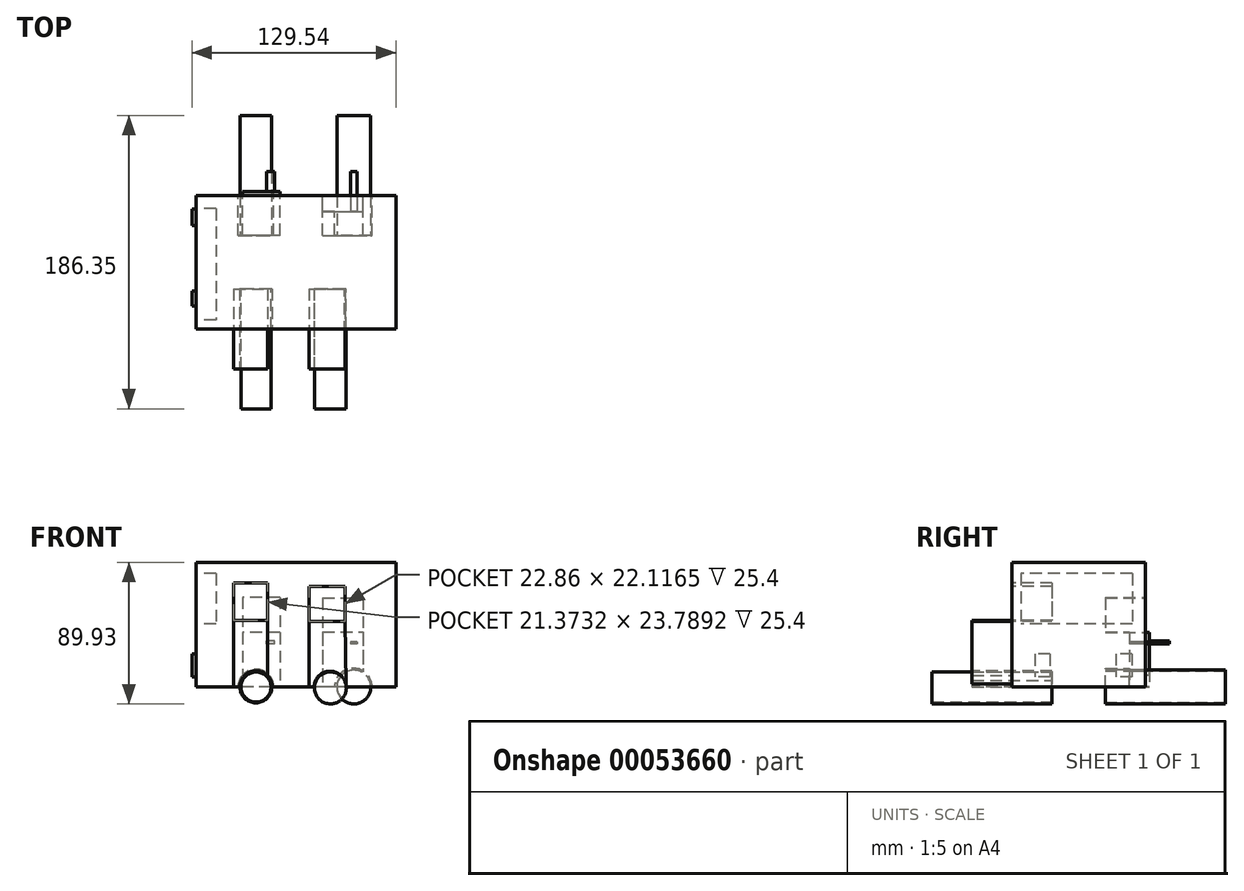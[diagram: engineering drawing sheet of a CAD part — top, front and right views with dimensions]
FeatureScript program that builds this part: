
annotation { "Feature Type Name" : "Feature", "Feature Type Description" : "" }
export const myFeature = defineFeature(function(context is Context, id is Id, definition is map)
    precondition{}
    {
        {
            var Q0;
            Q0=qCreatedBy(makeId("Right.planeOp"),FACE);
            var sketch = newSketch(context, id + "F0", { "sketchPlane" : qUnion([Q0])});
            skLineSegment(sketch, "E0.bottom", {"start": v(46.13, 54.55) * mm, "end": v(-38.62, 54.55) * mm});
            skLineSegment(sketch, "E0.top", {"start": v(46.13, -24.63) * mm, "end": v(-38.62, -24.63) * mm});
            skLineSegment(sketch, "E0.left", {"start": v(46.13, 54.55) * mm, "end": v(46.13, -24.63) * mm});
            skLineSegment(sketch, "E0.right", {"start": v(-38.62, 54.55) * mm, "end": v(-38.62, -24.63) * mm});
            skSolve(sketch);
        }
        {
            var Q0;
            Q0=makeQuery(id+"F0.imprint","IMPRINT",FACE,{"disambiguationData":[TD([[makeQuery(id+"F0.imprint","IMPRINT",EDGE,{"derivedFrom":sQuery(id+"F0.wireOp",EDGE,"E0.bottom")}),1.0]])]});
            extrude(context, id + "F1", {"entities" : qUnion([Q0]), "depth" : 127 * mm});
        }
        {
            var Q0;
            Q0=makeQuery(id+"F1.opExtrude","CAP_FACE",FACE,{"disambiguationData":[OSD([sQuery(id+"F0.wireOp",EDGE,"E0.bottom"),sQuery(id+"F0.wireOp",EDGE,"E0.top"),sQuery(id+"F0.wireOp",EDGE,"E0.left"),sQuery(id+"F0.wireOp",EDGE,"E0.right")])],"isStart":true});
            var sketch = newSketch(context, id + "F2", { "sketchPlane" : qUnion([Q0])});
            skLineSegment(sketch, "E1.bottom", {"start": v(-37.77, 47.49) * mm, "end": v(33.04, 47.49) * mm});
            skLineSegment(sketch, "E1.top", {"start": v(-37.77, 15.33) * mm, "end": v(33.04, 15.33) * mm});
            skLineSegment(sketch, "E1.left", {"start": v(-37.77, 47.49) * mm, "end": v(-37.77, 15.33) * mm});
            skLineSegment(sketch, "E1.right", {"start": v(33.04, 47.49) * mm, "end": v(33.04, 15.33) * mm});
            skSolve(sketch);
        }
        {
            var Q0;
            Q0=makeQuery(id+"F2.imprint","IMPRINT",FACE,{"disambiguationData":[TD([[makeQuery(id+"F2.imprint","IMPRINT",EDGE,{"derivedFrom":sQuery(id+"F2.wireOp",EDGE,"E1.bottom")}),-1.0]])]});
            extrude(context, id + "F3", {"entities" : qUnion([Q0]), "operationType" : NewBodyOperationType.REMOVE, "oppositeDirection" : true, "depth" : 12.7 * mm});
        }
        {
            var Q0;
            Q0=makeQuery(id+"F1.opExtrude","SWEPT_FACE",FACE,{"disambiguationData":[OSD([sQuery(id+"F0.wireOp",EDGE,"E0.left")])]});
            var sketch = newSketch(context, id + "F4", { "sketchPlane" : qUnion([Q0])});
            skCircle(sketch, "E2", {"center": v(-99.97, -24.63) * mm, "radius": 11.9 * mm});
            skCircle(sketch, "E3", {"center": v(-38.08, -24.63) * mm, "radius": 11.33 * mm});
            skLineSegment(sketch, "E4", {"start": v(-75.62, 13.1) * mm, "end": v(-75.62, -24.63) * mm});
            skLineSegment(sketch, "E5", {"start": v(-75.62, 13.1) * mm, "end": v(-75.62, 31.5) * mm});
            skLineSegment(sketch, "E6", {"start": v(-50.34, 30.39) * mm, "end": v(-49.4, -24.63) * mm});
            skLineSegment(sketch, "E7", {"start": v(-98.66, 30.39) * mm, "end": v(-98.66, -7.53) * mm});
            skLineSegment(sketch, "E8", {"start": v(-98.66, -7.53) * mm, "end": v(-98.66, -12.79) * mm});
            skSolve(sketch);
        }
        {
            var Q0;
            {var subQ0=sQuery(id+"F4.wireOp",EDGE,"E2");var subQ1=makeQuery(id+"F4.imprint","IMPRINT",VERTEX,{"derivedFrom":subQ0});Q0=makeQuery(id+"F4.imprint","IMPRINT",FACE,{"disambiguationData":[TD([[makeQuery(id+"F4.imprint","IMPRINT",EDGE,{"disambiguationData":[TD([[subQ1,1.0]])],"derivedFrom":subQ0}),1.0]])]});}
            var Q1;
            {var subQ0=sQuery(id+"F4.wireOp",EDGE,"E3");var subQ1=makeQuery(id+"F1.opExtrude","SWEPT_EDGE",EDGE,{"disambiguationData":[OSD([sQuery(id+"F0.wireOp",EDGE,"E0.top"),sQuery(id+"F0.wireOp",EDGE,"E0.left")])]});var subQ2=makeQuery(id+"F4.imprint","INTERSECT",VERTEX,{"disambiguationData":[OD(0.0)],"derivedFrom":[subQ1,subQ0]});Q1=makeQuery(id+"F4.imprint","IMPRINT",FACE,{"disambiguationData":[TD([[makeQuery(id+"F4.imprint","IMPRINT",EDGE,{"disambiguationData":[TD([[subQ2,-1.0]])],"derivedFrom":subQ0}),1.0]])]});}
            extrude(context, id + "F5", {"entities" : qUnion([Q0, Q1]), "operationType" : NewBodyOperationType.REMOVE, "oppositeDirection" : true, "depth" : 25.4 * mm});
        }
        {
            var Q0;
            Q0=makeQuery(id+"F1.opExtrude","SWEPT_FACE",FACE,{"disambiguationData":[OSD([sQuery(id+"F0.wireOp",EDGE,"E0.right")])]});
            var sketch = newSketch(context, id + "F6", { "sketchPlane" : qUnion([Q0])});
            skCircle(sketch, "E9", {"center": v(38.19, -24.63) * mm, "radius": 10.32 * mm});
            skCircle(sketch, "E10", {"center": v(85.2, -24.63) * mm, "radius": 10.06 * mm});
            skLineSegment(sketch, "E11", {"start": v(67, 17.75) * mm, "end": v(68.48, -24.63) * mm});
            skLineSegment(sketch, "E12", {"start": v(43.39, 16.82) * mm, "end": v(45.25, -14.22) * mm});
            skLineSegment(sketch, "E13", {"start": v(45.25, -14.22) * mm, "end": v(42.64, 29.28) * mm});
            skLineSegment(sketch, "E14", {"start": v(67, 17.75) * mm, "end": v(66.6, 29.13) * mm});
            skLineSegment(sketch, "E15", {"start": v(65.5, 29.83) * mm, "end": v(66.6, 29.13) * mm});
            skLineSegment(sketch, "E16", {"start": v(94.13, -19.99) * mm, "end": v(88.74, 26.86) * mm});
            skSolve(sketch);
        }
        {
            var Q0;
            {var subQ0=sQuery(id+"F6.wireOp",EDGE,"E9");var subQ1=makeQuery(id+"F1.opExtrude","SWEPT_EDGE",EDGE,{"disambiguationData":[OSD([sQuery(id+"F0.wireOp",EDGE,"E0.top"),sQuery(id+"F0.wireOp",EDGE,"E0.right")])]});var subQ2=makeQuery(id+"F6.imprint","INTERSECT",VERTEX,{"disambiguationData":[OD(0.0)],"derivedFrom":[subQ1,subQ0]});Q0=makeQuery(id+"F6.imprint","IMPRINT",FACE,{"disambiguationData":[TD([[makeQuery(id+"F6.imprint","IMPRINT",EDGE,{"disambiguationData":[TD([[subQ2,-1.0]])],"derivedFrom":subQ0}),1.0]])]});}
            var Q1;
            {var subQ0=sQuery(id+"F6.wireOp",EDGE,"E9");var subQ1=makeQuery(id+"F1.opExtrude","SWEPT_EDGE",EDGE,{"disambiguationData":[OSD([sQuery(id+"F0.wireOp",EDGE,"E0.top"),sQuery(id+"F0.wireOp",EDGE,"E0.right")])]});var subQ2=makeQuery(id+"F6.imprint","INTERSECT",VERTEX,{"disambiguationData":[OD(0.0)],"derivedFrom":[subQ1,subQ0]});Q1=makeQuery(id+"F6.imprint","IMPRINT",FACE,{"disambiguationData":[TD([[makeQuery(id+"F6.imprint","IMPRINT",EDGE,{"disambiguationData":[TD([[subQ2,1.0]])],"derivedFrom":subQ0}),1.0]])]});}
            var Q2;
            {var subQ0=sQuery(id+"F6.wireOp",EDGE,"E10");var subQ1=makeQuery(id+"F6.imprint","IMPRINT",VERTEX,{"derivedFrom":subQ0});Q2=makeQuery(id+"F6.imprint","IMPRINT",FACE,{"disambiguationData":[TD([[makeQuery(id+"F6.imprint","IMPRINT",EDGE,{"disambiguationData":[TD([[subQ1,1.0]])],"derivedFrom":subQ0}),1.0]])]});}
            extrude(context, id + "F7", {"entities" : qUnion([Q0, Q1, Q2]), "operationType" : NewBodyOperationType.REMOVE, "oppositeDirection" : true, "depth" : 25.4 * mm});
        }
        {
            var Q0;
            Q0=makeQuery(id+"F1.opExtrude","SWEPT_FACE",FACE,{"disambiguationData":[OSD([sQuery(id+"F0.wireOp",EDGE,"E0.right")])]});
            var sketch = newSketch(context, id + "F8", { "sketchPlane" : qUnion([Q0])});
            skLineSegment(sketch, "E17.bottom", {"start": v(24.06, 41.35) * mm, "end": v(45.43, 41.35) * mm});
            skLineSegment(sketch, "E17.top", {"start": v(24.06, 17.56) * mm, "end": v(45.43, 17.56) * mm});
            skLineSegment(sketch, "E17.left", {"start": v(24.06, 41.35) * mm, "end": v(24.06, 17.56) * mm});
            skLineSegment(sketch, "E17.right", {"start": v(45.43, 41.35) * mm, "end": v(45.43, 17.56) * mm});
            skLineSegment(sketch, "E18.bottom", {"start": v(71.83, 39.3) * mm, "end": v(94.69, 39.3) * mm});
            skLineSegment(sketch, "E18.top", {"start": v(71.83, 17.2) * mm, "end": v(94.69, 17.2) * mm});
            skLineSegment(sketch, "E18.left", {"start": v(71.83, 39.3) * mm, "end": v(71.83, 17.2) * mm});
            skLineSegment(sketch, "E18.right", {"start": v(94.69, 39.3) * mm, "end": v(94.69, 17.2) * mm});
            skSolve(sketch);
        }
        {
            var Q0;
            Q0=makeQuery(id+"F8.imprint","IMPRINT",FACE,{"disambiguationData":[TD([[makeQuery(id+"F8.imprint","IMPRINT",EDGE,{"derivedFrom":sQuery(id+"F8.wireOp",EDGE,"E17.bottom")}),-1.0]])]});
            var Q1;
            Q1=makeQuery(id+"F8.imprint","IMPRINT",FACE,{"disambiguationData":[TD([[makeQuery(id+"F8.imprint","IMPRINT",EDGE,{"derivedFrom":sQuery(id+"F8.wireOp",EDGE,"E18.bottom")}),-1.0]])]});
            extrude(context, id + "F9", {"entities" : qUnion([Q0, Q1]), "operationType" : NewBodyOperationType.REMOVE, "oppositeDirection" : true, "depth" : 25.4 * mm});
        }
        {
            var Q0;
            Q0=makeQuery(id+"F1.opExtrude","SWEPT_FACE",FACE,{"disambiguationData":[OSD([sQuery(id+"F0.wireOp",EDGE,"E0.left")])]});
            var sketch = newSketch(context, id + "F10", { "sketchPlane" : qUnion([Q0])});
            skLineSegment(sketch, "E19.bottom", {"start": v(-53.5, 32.43) * mm, "end": v(-29.53, 32.43) * mm});
            skLineSegment(sketch, "E19.top", {"start": v(-53.5, 9.94) * mm, "end": v(-29.53, 9.94) * mm});
            skLineSegment(sketch, "E19.left", {"start": v(-53.5, 32.43) * mm, "end": v(-53.5, 9.94) * mm});
            skLineSegment(sketch, "E19.right", {"start": v(-29.53, 32.43) * mm, "end": v(-29.53, 9.94) * mm});
            skLineSegment(sketch, "E20.bottom", {"start": v(-80.45, 31.87) * mm, "end": v(-106.1, 31.87) * mm});
            skLineSegment(sketch, "E20.top", {"start": v(-80.45, 10.31) * mm, "end": v(-106.1, 10.31) * mm});
            skLineSegment(sketch, "E20.left", {"start": v(-80.45, 31.87) * mm, "end": v(-80.45, 10.31) * mm});
            skLineSegment(sketch, "E20.right", {"start": v(-106.1, 31.87) * mm, "end": v(-106.1, 10.31) * mm});
            skSolve(sketch);
        }
        {
            var Q0;
            Q0=makeQuery(id+"F10.imprint","IMPRINT",FACE,{"disambiguationData":[TD([[makeQuery(id+"F10.imprint","IMPRINT",EDGE,{"derivedFrom":sQuery(id+"F10.wireOp",EDGE,"E20.bottom")}),1.0]])]});
            var Q1;
            Q1=makeQuery(id+"F10.imprint","IMPRINT",FACE,{"disambiguationData":[TD([[makeQuery(id+"F10.imprint","IMPRINT",EDGE,{"derivedFrom":sQuery(id+"F10.wireOp",EDGE,"E19.bottom")}),-1.0]])]});
            extrude(context, id + "F11", {"entities" : qUnion([Q0, Q1]), "operationType" : NewBodyOperationType.REMOVE, "oppositeDirection" : true, "depth" : 25.4 * mm});
        }
        {
            var Q0;
            Q0=makeQuery(id+"F1.opExtrude","CAP_FACE",FACE,{"disambiguationData":[OSD([sQuery(id+"F0.wireOp",EDGE,"E0.bottom"),sQuery(id+"F0.wireOp",EDGE,"E0.top"),sQuery(id+"F0.wireOp",EDGE,"E0.left"),sQuery(id+"F0.wireOp",EDGE,"E0.right")])],"isStart":true});
            var sketch = newSketch(context, id + "F12", { "sketchPlane" : qUnion([Q0])});
            skLineSegment(sketch, "E21.bottom", {"start": v(-37.58, -3.44) * mm, "end": v(-27.17, -3.44) * mm});
            skLineSegment(sketch, "E21.top", {"start": v(-37.58, -18.12) * mm, "end": v(-27.17, -18.12) * mm});
            skLineSegment(sketch, "E21.left", {"start": v(-37.58, -3.44) * mm, "end": v(-37.58, -18.12) * mm});
            skLineSegment(sketch, "E21.right", {"start": v(-27.17, -3.44) * mm, "end": v(-27.17, -18.12) * mm});
            skLineSegment(sketch, "E22.bottom", {"start": v(14.46, -3.62) * mm, "end": v(24.12, -3.62) * mm});
            skLineSegment(sketch, "E22.top", {"start": v(14.46, -18.3) * mm, "end": v(24.12, -18.3) * mm});
            skLineSegment(sketch, "E22.left", {"start": v(14.46, -3.62) * mm, "end": v(14.46, -18.3) * mm});
            skLineSegment(sketch, "E22.right", {"start": v(24.12, -3.62) * mm, "end": v(24.12, -18.3) * mm});
            skSolve(sketch);
        }
        {
            var Q0;
            Q0=makeQuery(id+"F12.imprint","IMPRINT",FACE,{"disambiguationData":[TD([[makeQuery(id+"F12.imprint","IMPRINT",EDGE,{"derivedFrom":sQuery(id+"F12.wireOp",EDGE,"E21.bottom")}),-1.0]])]});
            var Q1;
            Q1=makeQuery(id+"F12.imprint","IMPRINT",FACE,{"disambiguationData":[TD([[makeQuery(id+"F12.imprint","IMPRINT",EDGE,{"derivedFrom":sQuery(id+"F12.wireOp",EDGE,"E22.bottom")}),-1.0]])]});
            extrude(context, id + "F13", {"entities" : qUnion([Q0, Q1]), "operationType" : NewBodyOperationType.ADD, "depth" : 2.54 * mm});
        }
        {
            var Q0;
            Q0=makeQuery(id+"F1.opExtrude","SWEPT_FACE",FACE,{"disambiguationData":[OSD([sQuery(id+"F0.wireOp",EDGE,"E0.left")])]});
            var sketch = newSketch(context, id + "F14", { "sketchPlane" : qUnion([Q0])});
            skLineSegment(sketch, "E23", {"start": v(-53.5, 30.57) * mm, "end": v(-53.5, -24.63) * mm});
            skLineSegment(sketch, "E24", {"start": v(-80.45, 31.87) * mm, "end": v(-80.45, -24.63) * mm});
            skLineSegment(sketch, "E25", {"start": v(-29.53, 9.94) * mm, "end": v(-29.53, -17.2) * mm});
            skLineSegment(sketch, "E26", {"start": v(-106.1, 10.31) * mm, "end": v(-106.1, -14.42) * mm});
            skSolve(sketch);
        }
        {
            var Q0;
            {var subQ6=sQuery(id+"F14.wireOp",EDGE,"E25");Q0=makeQuery(id+"F14.imprint","IMPRINT",FACE,{"disambiguationData":[TD([[makeQuery(id+"F14.imprint","IMPRINT",EDGE,{"derivedFrom":subQ6}),-1.0]])]});}
            var Q1;
            {var subQ6=sQuery(id+"F14.wireOp",EDGE,"E26");Q1=makeQuery(id+"F14.imprint","IMPRINT",FACE,{"disambiguationData":[TD([[makeQuery(id+"F14.imprint","IMPRINT",EDGE,{"derivedFrom":subQ6}),1.0]])]});}
            extrude(context, id + "F15", {"entities" : qUnion([Q0, Q1]), "operationType" : NewBodyOperationType.ADD, "depth" : 2.54 * mm});
        }
        {
            var Q0;
            Q0=makeQuery(id+"F15.opExtrude","CAP_FACE",FACE,{"disambiguationData":[OSD([sQuery(id+"F0.wireOp",EDGE,"E0.top"),sQuery(id+"F0.wireOp",EDGE,"E0.left"),sQuery(id+"F4.wireOp",EDGE,"E2"),sQuery(id+"F10.wireOp",EDGE,"E20.top"),sQuery(id+"F14.wireOp",EDGE,"E24"),sQuery(id+"F14.wireOp",EDGE,"E26")])],"isStart":false});
            var sketch = newSketch(context, id + "F16", { "sketchPlane" : qUnion([Q0])});
            skLineSegment(sketch, "E27.bottom", {"start": v(-102.38, 4.18) * mm, "end": v(-98.1, 4.18) * mm});
            skLineSegment(sketch, "E27.top", {"start": v(-102.38, 2.7) * mm, "end": v(-98.1, 2.7) * mm});
            skLineSegment(sketch, "E27.left", {"start": v(-102.38, 4.18) * mm, "end": v(-102.38, 2.7) * mm});
            skLineSegment(sketch, "E27.right", {"start": v(-98.1, 4.18) * mm, "end": v(-98.1, 2.7) * mm});
            skLineSegment(sketch, "E28.bottom", {"start": v(-49.97, 2.7) * mm, "end": v(-44.95, 2.7) * mm});
            skLineSegment(sketch, "E28.top", {"start": v(-49.97, 4.55) * mm, "end": v(-44.95, 4.55) * mm});
            skLineSegment(sketch, "E28.left", {"start": v(-49.97, 2.7) * mm, "end": v(-49.97, 4.55) * mm});
            skLineSegment(sketch, "E28.right", {"start": v(-44.95, 2.7) * mm, "end": v(-44.95, 4.55) * mm});
            skSolve(sketch);
        }
        {
            var Q0;
            Q0=makeQuery(id+"F16.imprint","IMPRINT",FACE,{"disambiguationData":[TD([[makeQuery(id+"F16.imprint","IMPRINT",EDGE,{"derivedFrom":sQuery(id+"F16.wireOp",EDGE,"E27.bottom")}),-1.0]])]});
            var Q1;
            Q1=makeQuery(id+"F16.imprint","IMPRINT",FACE,{"disambiguationData":[TD([[makeQuery(id+"F16.imprint","IMPRINT",EDGE,{"derivedFrom":sQuery(id+"F16.wireOp",EDGE,"E28.bottom")}),1.0]])]});
            extrude(context, id + "F17", {"entities" : qUnion([Q0, Q1]), "operationType" : NewBodyOperationType.ADD, "depth" : 12.7 * mm});
        }
        {
            var Q0;
            Q0=makeQuery(id+"F17.opExtrude","CAP_FACE",FACE,{"disambiguationData":[OSD([sQuery(id+"F16.wireOp",EDGE,"E27.bottom"),sQuery(id+"F16.wireOp",EDGE,"E27.top"),sQuery(id+"F16.wireOp",EDGE,"E27.left"),sQuery(id+"F16.wireOp",EDGE,"E27.right")])],"isStart":false});
            var Q1;
            Q1=makeQuery(id+"F17.opExtrude","CAP_FACE",FACE,{"disambiguationData":[OSD([sQuery(id+"F16.wireOp",EDGE,"E28.bottom"),sQuery(id+"F16.wireOp",EDGE,"E28.top"),sQuery(id+"F16.wireOp",EDGE,"E28.left"),sQuery(id+"F16.wireOp",EDGE,"E28.right")])],"isStart":false});
            extrude(context, id + "F18", {"entities" : qUnion([Q0, Q1]), "operationType" : NewBodyOperationType.ADD, "depth" : 12.7 * mm});
        }
        {
            var Q0;
            Q0=makeQuery(id+"F15.opExtrude","CAP_FACE",FACE,{"disambiguationData":[OSD([sQuery(id+"F0.wireOp",EDGE,"E0.top"),sQuery(id+"F0.wireOp",EDGE,"E0.left"),sQuery(id+"F4.wireOp",EDGE,"E2"),sQuery(id+"F10.wireOp",EDGE,"E20.top"),sQuery(id+"F14.wireOp",EDGE,"E24"),sQuery(id+"F14.wireOp",EDGE,"E26")])],"isStart":false});
            var Q1;
            Q1=makeQuery(id+"F18.opExtrude","CAP_FACE",FACE,{"disambiguationData":[OSD([sQuery(id+"F16.wireOp",EDGE,"E28.bottom"),sQuery(id+"F16.wireOp",EDGE,"E28.top"),sQuery(id+"F16.wireOp",EDGE,"E28.left"),sQuery(id+"F16.wireOp",EDGE,"E28.right")])],"isStart":false});
            var Q2;
            Q2=makeQuery(id+"F18.opExtrude","CAP_FACE",FACE,{"disambiguationData":[OSD([sQuery(id+"F16.wireOp",EDGE,"E27.bottom"),sQuery(id+"F16.wireOp",EDGE,"E27.top"),sQuery(id+"F16.wireOp",EDGE,"E27.left"),sQuery(id+"F16.wireOp",EDGE,"E27.right")])],"isStart":false});
            extrude(context, id + "F19", {"entities" : qUnion([Q0, Q1, Q2]), "operationType" : NewBodyOperationType.REMOVE, "oppositeDirection" : true, "depth" : 12.7 * mm});
        }
        {
            var Q0;
            Q0=makeQuery(id+"F1.opExtrude","SWEPT_FACE",FACE,{"disambiguationData":[OSD([sQuery(id+"F0.wireOp",EDGE,"E0.right")])]});
            var sketch = newSketch(context, id + "F20", { "sketchPlane" : qUnion([Q0])});
            skLineSegment(sketch, "E29", {"start": v(45.43, 17.56) * mm, "end": v(45.43, -17.28) * mm});
            skLineSegment(sketch, "E30", {"start": v(24.06, 17.56) * mm, "end": v(24.06, -24.63) * mm});
            skLineSegment(sketch, "E31", {"start": v(71.83, 17.2) * mm, "end": v(71.83, -24.63) * mm});
            skLineSegment(sketch, "E32", {"start": v(94.69, 17.2) * mm, "end": v(95.27, -24.63) * mm});
            skSolve(sketch);
        }
        {
            var Q0;
            {var subQ6=sQuery(id+"F20.wireOp",EDGE,"E29");Q0=makeQuery(id+"F20.imprint","IMPRINT",FACE,{"disambiguationData":[TD([[makeQuery(id+"F20.imprint","IMPRINT",EDGE,{"derivedFrom":subQ6}),-1.0]])]});}
            var Q1;
            {var subQ9=sQuery(id+"F20.wireOp",EDGE,"E31");Q1=makeQuery(id+"F20.imprint","IMPRINT",FACE,{"disambiguationData":[TD([[makeQuery(id+"F20.imprint","IMPRINT",EDGE,{"derivedFrom":subQ9}),1.0]])]});}
            extrude(context, id + "F21", {"entities" : qUnion([Q0, Q1]), "operationType" : NewBodyOperationType.ADD, "depth" : 12.7 * mm});
        }
        {
            var Q0;
            Q0=makeQuery(id+"F21.opExtrude","CAP_FACE",FACE,{"disambiguationData":[OSD([sQuery(id+"F0.wireOp",EDGE,"E0.top"),sQuery(id+"F0.wireOp",EDGE,"E0.right"),sQuery(id+"F6.wireOp",EDGE,"E9"),sQuery(id+"F8.wireOp",EDGE,"E17.top"),sQuery(id+"F20.wireOp",EDGE,"E29"),sQuery(id+"F20.wireOp",EDGE,"E30")])],"isStart":false});
            var Q1;
            Q1=makeQuery(id+"F21.opExtrude","CAP_FACE",FACE,{"disambiguationData":[OSD([sQuery(id+"F0.wireOp",EDGE,"E0.top"),sQuery(id+"F0.wireOp",EDGE,"E0.right"),sQuery(id+"F6.wireOp",EDGE,"E10"),sQuery(id+"F8.wireOp",EDGE,"E18.top"),sQuery(id+"F20.wireOp",EDGE,"E31"),sQuery(id+"F20.wireOp",EDGE,"E32")])],"isStart":false});
            extrude(context, id + "F22", {"entities" : qUnion([Q0, Q1]), "operationType" : NewBodyOperationType.ADD, "depth" : 12.7 * mm});
        }
        {
            var Q0;
            Q0=makeQuery(id+"F7.boolean.opBoolean","COPY",FACE,{"derivedFrom":makeQuery(id+"F7.opExtrude","CAP_FACE",FACE,{"disambiguationData":[OSD([sQuery(id+"F6.wireOp",EDGE,"E9")])],"isStart":false})});
            var sketch = newSketch(context, id + "F23", { "sketchPlane" : qUnion([Q0])});
            skCircle(sketch, "E33", {"center": v(38.19, -24.63) * mm, "radius": 9.54 * mm});
            skCircle(sketch, "E34", {"center": v(85.4, -25.18) * mm, "radius": 10.14 * mm});
            skSolve(sketch);
        }
        {
            var Q0;
            {var subQ0=sQuery(id+"F23.wireOp",EDGE,"E33");var subQ1=makeQuery(id+"F7.boolean.opBoolean","INTERSECT",EDGE,{"derivedFrom":[makeQuery(id+"F1.opExtrude","SWEPT_FACE",FACE,{"disambiguationData":[OSD([sQuery(id+"F0.wireOp",EDGE,"E0.top")])]}),makeQuery(id+"F7.opExtrude","CAP_FACE",FACE,{"disambiguationData":[OSD([sQuery(id+"F6.wireOp",EDGE,"E9")])],"isStart":false})]});var subQ2=makeQuery(id+"F23.imprint","INTERSECT",VERTEX,{"disambiguationData":[OD(0.0)],"derivedFrom":[subQ1,subQ0]});Q0=makeQuery(id+"F23.imprint","IMPRINT",FACE,{"disambiguationData":[TD([[makeQuery(id+"F23.imprint","IMPRINT",EDGE,{"disambiguationData":[TD([[subQ2,-1.0]])],"derivedFrom":subQ0}),1.0]])]});}
            var Q1;
            Q1=makeQuery(id+"F23.imprint","IMPRINT",FACE,{"disambiguationData":[TD([[makeQuery(id+"F23.imprint","IMPRINT",EDGE,{"derivedFrom":sQuery(id+"F23.wireOp",EDGE,"E34")}),1.0]])]});
            var Q2;
            {var subQ0=sQuery(id+"F23.wireOp",EDGE,"E33");var subQ1=makeQuery(id+"F7.boolean.opBoolean","INTERSECT",EDGE,{"derivedFrom":[makeQuery(id+"F1.opExtrude","SWEPT_FACE",FACE,{"disambiguationData":[OSD([sQuery(id+"F0.wireOp",EDGE,"E0.top")])]}),makeQuery(id+"F7.opExtrude","CAP_FACE",FACE,{"disambiguationData":[OSD([sQuery(id+"F6.wireOp",EDGE,"E9")])],"isStart":false})]});var subQ2=makeQuery(id+"F23.imprint","INTERSECT",VERTEX,{"disambiguationData":[OD(0.0)],"derivedFrom":[subQ1,subQ0]});Q2=makeQuery(id+"F23.imprint","IMPRINT",FACE,{"disambiguationData":[TD([[makeQuery(id+"F23.imprint","IMPRINT",EDGE,{"disambiguationData":[TD([[subQ2,1.0]])],"derivedFrom":subQ0}),1.0]])]});}
            extrude(context, id + "F24", {"entities" : qUnion([Q0, Q1, Q2]), "operationType" : NewBodyOperationType.ADD, "depth" : 76.2 * mm});
        }
        {
            var Q0;
            Q0=makeQuery(id+"F5.boolean.opBoolean","COPY",FACE,{"derivedFrom":makeQuery(id+"F5.opExtrude","CAP_FACE",FACE,{"disambiguationData":[OSD([sQuery(id+"F0.wireOp",EDGE,"E0.top"),sQuery(id+"F0.wireOp",EDGE,"E0.left"),sQuery(id+"F4.wireOp",EDGE,"E3")])],"isStart":false})});
            var sketch = newSketch(context, id + "F25", { "sketchPlane" : qUnion([Q0])});
            skCircle(sketch, "E35", {"center": v(-100.34, -24.63) * mm, "radius": 10.76 * mm});
            skCircle(sketch, "E36", {"center": v(-38.08, -24.63) * mm, "radius": 10.04 * mm});
            skSolve(sketch);
        }
        {
            var Q0;
            Q0=makeQuery(id+"F25.imprint","IMPRINT",FACE,{"disambiguationData":[TD([[makeQuery(id+"F25.imprint","IMPRINT",EDGE,{"derivedFrom":sQuery(id+"F25.wireOp",EDGE,"E35")}),1.0]])]});
            var Q1;
            {var subQ0=sQuery(id+"F25.wireOp",EDGE,"E36");var subQ1=sQuery(id+"F4.wireOp",EDGE,"E3");var subQ2=sQuery(id+"F0.wireOp",EDGE,"E0.left");var subQ3=sQuery(id+"F0.wireOp",EDGE,"E0.top");var subQ4=makeQuery(id+"F1.opExtrude","SWEPT_EDGE",EDGE,{"disambiguationData":[OSD([subQ3,subQ2])]});var subQ5=makeQuery(id+"F5.boolean.opBoolean","COPY",EDGE,{"derivedFrom":makeQuery(id+"F5.opExtrude","CAP_EDGE",EDGE,{"disambiguationData":[OSD([subQ3,subQ2]),TDD([makeQuery(id+"F4.imprint","IMPRINT",EDGE,{"disambiguationData":[TD([[makeQuery(id+"F4.imprint","INTERSECT",VERTEX,{"disambiguationData":[OD(0.0)],"derivedFrom":[subQ4,subQ1]}),1.0]])],"derivedFrom":subQ4})])],"isStart":false})});var subQ6=makeQuery(id+"F25.imprint","INTERSECT",VERTEX,{"disambiguationData":[OD(0.0)],"derivedFrom":[subQ5,subQ0]});Q1=makeQuery(id+"F25.imprint","IMPRINT",FACE,{"disambiguationData":[TD([[makeQuery(id+"F25.imprint","IMPRINT",EDGE,{"disambiguationData":[TD([[subQ6,1.0]])],"derivedFrom":subQ0}),1.0]])]});}
            var Q2;
            {var subQ0=sQuery(id+"F25.wireOp",EDGE,"E36");var subQ1=sQuery(id+"F4.wireOp",EDGE,"E3");var subQ2=sQuery(id+"F0.wireOp",EDGE,"E0.left");var subQ3=sQuery(id+"F0.wireOp",EDGE,"E0.top");var subQ4=makeQuery(id+"F1.opExtrude","SWEPT_EDGE",EDGE,{"disambiguationData":[OSD([subQ3,subQ2])]});var subQ5=makeQuery(id+"F5.boolean.opBoolean","COPY",EDGE,{"derivedFrom":makeQuery(id+"F5.opExtrude","CAP_EDGE",EDGE,{"disambiguationData":[OSD([subQ3,subQ2]),TDD([makeQuery(id+"F4.imprint","IMPRINT",EDGE,{"disambiguationData":[TD([[makeQuery(id+"F4.imprint","INTERSECT",VERTEX,{"disambiguationData":[OD(0.0)],"derivedFrom":[subQ4,subQ1]}),1.0]])],"derivedFrom":subQ4})])],"isStart":false})});var subQ6=makeQuery(id+"F25.imprint","INTERSECT",VERTEX,{"disambiguationData":[OD(0.0)],"derivedFrom":[subQ5,subQ0]});Q2=makeQuery(id+"F25.imprint","IMPRINT",FACE,{"disambiguationData":[TD([[makeQuery(id+"F25.imprint","IMPRINT",EDGE,{"disambiguationData":[TD([[subQ6,-1.0]])],"derivedFrom":subQ0}),1.0]])]});}
            extrude(context, id + "F26", {"entities" : qUnion([Q0, Q1, Q2]), "operationType" : NewBodyOperationType.ADD, "depth" : 76.2 * mm});
        }
    });
